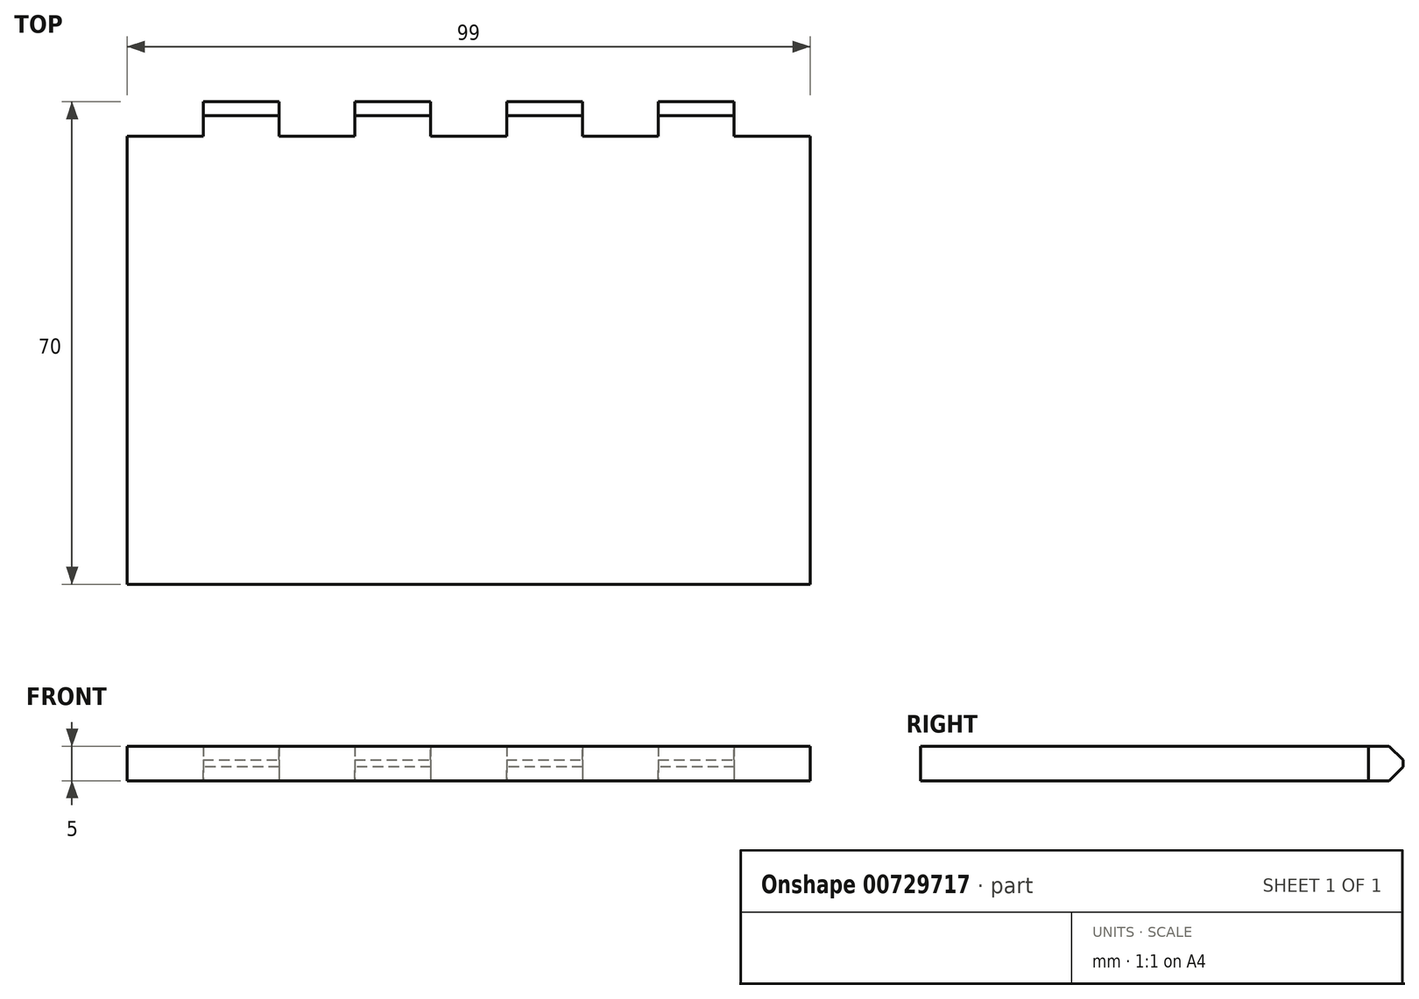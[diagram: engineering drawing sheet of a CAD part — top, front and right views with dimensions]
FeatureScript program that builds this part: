
annotation { "Feature Type Name" : "Feature", "Feature Type Description" : "" }
export const myFeature = defineFeature(function(context is Context, id is Id, definition is map)
    precondition{}
    {
        {
            var Q0;
            Q0=qCreatedBy(makeId("Top.planeOp"),FACE);
            var sketch = newSketch(context, id + "F0", { "sketchPlane" : qUnion([Q0])});
            skLineSegment(sketch, "E0.bottom", {"start": v(49.5, 35) * mm, "end": v(-49.5, 35) * mm});
            skLineSegment(sketch, "E0.top", {"start": v(49.5, -35) * mm, "end": v(-49.5, -35) * mm});
            skLineSegment(sketch, "E0.left", {"start": v(49.5, 35) * mm, "end": v(49.5, -35) * mm});
            skLineSegment(sketch, "E0.right", {"start": v(-49.5, 35) * mm, "end": v(-49.5, -35) * mm});
            skPoint(sketch, "E0.middle", {"position": v(0, 0) * mm});
            skLineSegment(sketch, "E1.bottom", {"start": v(-49.5, 35) * mm, "end": v(-38.5, 35) * mm});
            skLineSegment(sketch, "E1.top", {"start": v(-49.5, 30) * mm, "end": v(-38.5, 30) * mm});
            skLineSegment(sketch, "E1.left", {"start": v(-49.5, 35) * mm, "end": v(-49.5, 30) * mm});
            skLineSegment(sketch, "E1.right", {"start": v(-38.5, 35) * mm, "end": v(-38.5, 30) * mm});
            skLineSegment(sketch, "E2.1.0.0", {"start": v(-27.5, 30) * mm, "end": v(-16.5, 30) * mm});
            skLineSegment(sketch, "E2.1.0.1", {"start": v(-16.5, 35) * mm, "end": v(-16.5, 30) * mm});
            skLineSegment(sketch, "E2.1.0.2", {"start": v(-27.5, 35) * mm, "end": v(-16.5, 35) * mm});
            skLineSegment(sketch, "E2.1.0.3", {"start": v(-27.5, 35) * mm, "end": v(-27.5, 30) * mm});
            skLineSegment(sketch, "E2.2.0.0", {"start": v(-5.5, 30) * mm, "end": v(5.5, 30) * mm});
            skLineSegment(sketch, "E2.2.0.1", {"start": v(5.5, 35) * mm, "end": v(5.5, 30) * mm});
            skLineSegment(sketch, "E2.2.0.2", {"start": v(-5.5, 35) * mm, "end": v(5.5, 35) * mm});
            skLineSegment(sketch, "E2.2.0.3", {"start": v(-5.5, 35) * mm, "end": v(-5.5, 30) * mm});
            skLineSegment(sketch, "E2.3.0.0", {"start": v(16.5, 30) * mm, "end": v(27.5, 30) * mm});
            skLineSegment(sketch, "E2.3.0.1", {"start": v(27.5, 35) * mm, "end": v(27.5, 30) * mm});
            skLineSegment(sketch, "E2.3.0.2", {"start": v(16.5, 35) * mm, "end": v(27.5, 35) * mm});
            skLineSegment(sketch, "E2.3.0.3", {"start": v(16.5, 35) * mm, "end": v(16.5, 30) * mm});
            skLineSegment(sketch, "E2.4.0.0", {"start": v(38.5, 30) * mm, "end": v(49.5, 30) * mm});
            skLineSegment(sketch, "E2.4.0.1", {"start": v(49.5, 35) * mm, "end": v(49.5, 30) * mm});
            skLineSegment(sketch, "E2.4.0.2", {"start": v(38.5, 35) * mm, "end": v(49.5, 35) * mm});
            skLineSegment(sketch, "E2.4.0.3", {"start": v(38.5, 35) * mm, "end": v(38.5, 30) * mm});
            skLineSegment(sketch, "E2.direction1", {"start": v(-49.5, 30) * mm, "end": v(-27.5, 30) * mm, "construction": true});
            skSolve(sketch);
        }
        {
            var Q0;
            Q0=makeQuery(id+"F0.imprint","IMPRINT",FACE,{"disambiguationData":[TD([[makeQuery(id+"F0.imprint","IMPRINT",EDGE,{"derivedFrom":sQuery(id+"F0.wireOp",EDGE,"E0.top")}),-1.0]])]});
            extrude(context, id + "F1", {"entities" : qUnion([Q0]), "depth" : 5 * mm, "offsetDistance" : 25 * mm});
        }
        {
            var Q0;
            {var subQ0=sQuery(id+"F0.wireOp",EDGE,"E0.bottom");Q0=makeQuery(id+"F1.opExtrude","CAP_EDGE",EDGE,{"disambiguationData":[OSD([subQ0]),TDD([makeQuery(id+"F0.imprint","IMPRINT",EDGE,{"disambiguationData":[TD([[makeQuery(id+"F0.imprint","INTERSECT",VERTEX,{"derivedFrom":[subQ0,sQuery(id+"F0.wireOp",EDGE,"E2.4.0.2"),sQuery(id+"F0.wireOp",EDGE,"E2.4.0.3")]}),-1.0]])],"derivedFrom":subQ0})])],"isStart":false});}
            var Q1;
            {var subQ0=sQuery(id+"F0.wireOp",EDGE,"E0.bottom");Q1=makeQuery(id+"F1.opExtrude","CAP_EDGE",EDGE,{"disambiguationData":[OSD([subQ0]),TDD([makeQuery(id+"F0.imprint","IMPRINT",EDGE,{"disambiguationData":[TD([[makeQuery(id+"F0.imprint","INTERSECT",VERTEX,{"derivedFrom":[subQ0,sQuery(id+"F0.wireOp",EDGE,"E2.2.0.1"),sQuery(id+"F0.wireOp",EDGE,"E2.2.0.2")]}),1.0]])],"derivedFrom":subQ0})])],"isStart":false});}
            var Q2;
            {var subQ0=sQuery(id+"F0.wireOp",EDGE,"E0.bottom");Q2=makeQuery(id+"F1.opExtrude","CAP_EDGE",EDGE,{"disambiguationData":[OSD([subQ0]),TDD([makeQuery(id+"F0.imprint","IMPRINT",EDGE,{"disambiguationData":[TD([[makeQuery(id+"F0.imprint","INTERSECT",VERTEX,{"derivedFrom":[subQ0,sQuery(id+"F0.wireOp",EDGE,"E2.1.0.1"),sQuery(id+"F0.wireOp",EDGE,"E2.1.0.2")]}),1.0]])],"derivedFrom":subQ0})])],"isStart":false});}
            var Q3;
            {var subQ0=sQuery(id+"F0.wireOp",EDGE,"E0.bottom");Q3=makeQuery(id+"F1.opExtrude","CAP_EDGE",EDGE,{"disambiguationData":[OSD([subQ0]),TDD([makeQuery(id+"F0.imprint","IMPRINT",EDGE,{"disambiguationData":[TD([[makeQuery(id+"F0.imprint","INTERSECT",VERTEX,{"derivedFrom":[subQ0,sQuery(id+"F0.wireOp",EDGE,"E1.bottom"),sQuery(id+"F0.wireOp",EDGE,"E1.right")]}),1.0]])],"derivedFrom":subQ0})])],"isStart":false});}
            var Q4;
            {var subQ0=sQuery(id+"F0.wireOp",EDGE,"E0.bottom");Q4=makeQuery(id+"F1.opExtrude","CAP_EDGE",EDGE,{"disambiguationData":[OSD([subQ0]),TDD([makeQuery(id+"F0.imprint","IMPRINT",EDGE,{"disambiguationData":[TD([[makeQuery(id+"F0.imprint","INTERSECT",VERTEX,{"derivedFrom":[subQ0,sQuery(id+"F0.wireOp",EDGE,"E1.bottom"),sQuery(id+"F0.wireOp",EDGE,"E1.right")]}),1.0]])],"derivedFrom":subQ0})])],"isStart":true});}
            var Q5;
            {var subQ0=sQuery(id+"F0.wireOp",EDGE,"E0.bottom");Q5=makeQuery(id+"F1.opExtrude","CAP_EDGE",EDGE,{"disambiguationData":[OSD([subQ0]),TDD([makeQuery(id+"F0.imprint","IMPRINT",EDGE,{"disambiguationData":[TD([[makeQuery(id+"F0.imprint","INTERSECT",VERTEX,{"derivedFrom":[subQ0,sQuery(id+"F0.wireOp",EDGE,"E2.1.0.1"),sQuery(id+"F0.wireOp",EDGE,"E2.1.0.2")]}),1.0]])],"derivedFrom":subQ0})])],"isStart":true});}
            var Q6;
            {var subQ0=sQuery(id+"F0.wireOp",EDGE,"E0.bottom");Q6=makeQuery(id+"F1.opExtrude","CAP_EDGE",EDGE,{"disambiguationData":[OSD([subQ0]),TDD([makeQuery(id+"F0.imprint","IMPRINT",EDGE,{"disambiguationData":[TD([[makeQuery(id+"F0.imprint","INTERSECT",VERTEX,{"derivedFrom":[subQ0,sQuery(id+"F0.wireOp",EDGE,"E2.2.0.1"),sQuery(id+"F0.wireOp",EDGE,"E2.2.0.2")]}),1.0]])],"derivedFrom":subQ0})])],"isStart":true});}
            var Q7;
            {var subQ0=sQuery(id+"F0.wireOp",EDGE,"E0.bottom");Q7=makeQuery(id+"F1.opExtrude","CAP_EDGE",EDGE,{"disambiguationData":[OSD([subQ0]),TDD([makeQuery(id+"F0.imprint","IMPRINT",EDGE,{"disambiguationData":[TD([[makeQuery(id+"F0.imprint","INTERSECT",VERTEX,{"derivedFrom":[subQ0,sQuery(id+"F0.wireOp",EDGE,"E2.4.0.2"),sQuery(id+"F0.wireOp",EDGE,"E2.4.0.3")]}),-1.0]])],"derivedFrom":subQ0})])],"isStart":true});}
            chamfer(context, id + "F2", {"entities" : qUnion([Q0, Q1, Q2, Q3, Q4, Q5, Q6, Q7]), "width" : 2 * mm, "tangentPropagation" : true});
        }
    });
